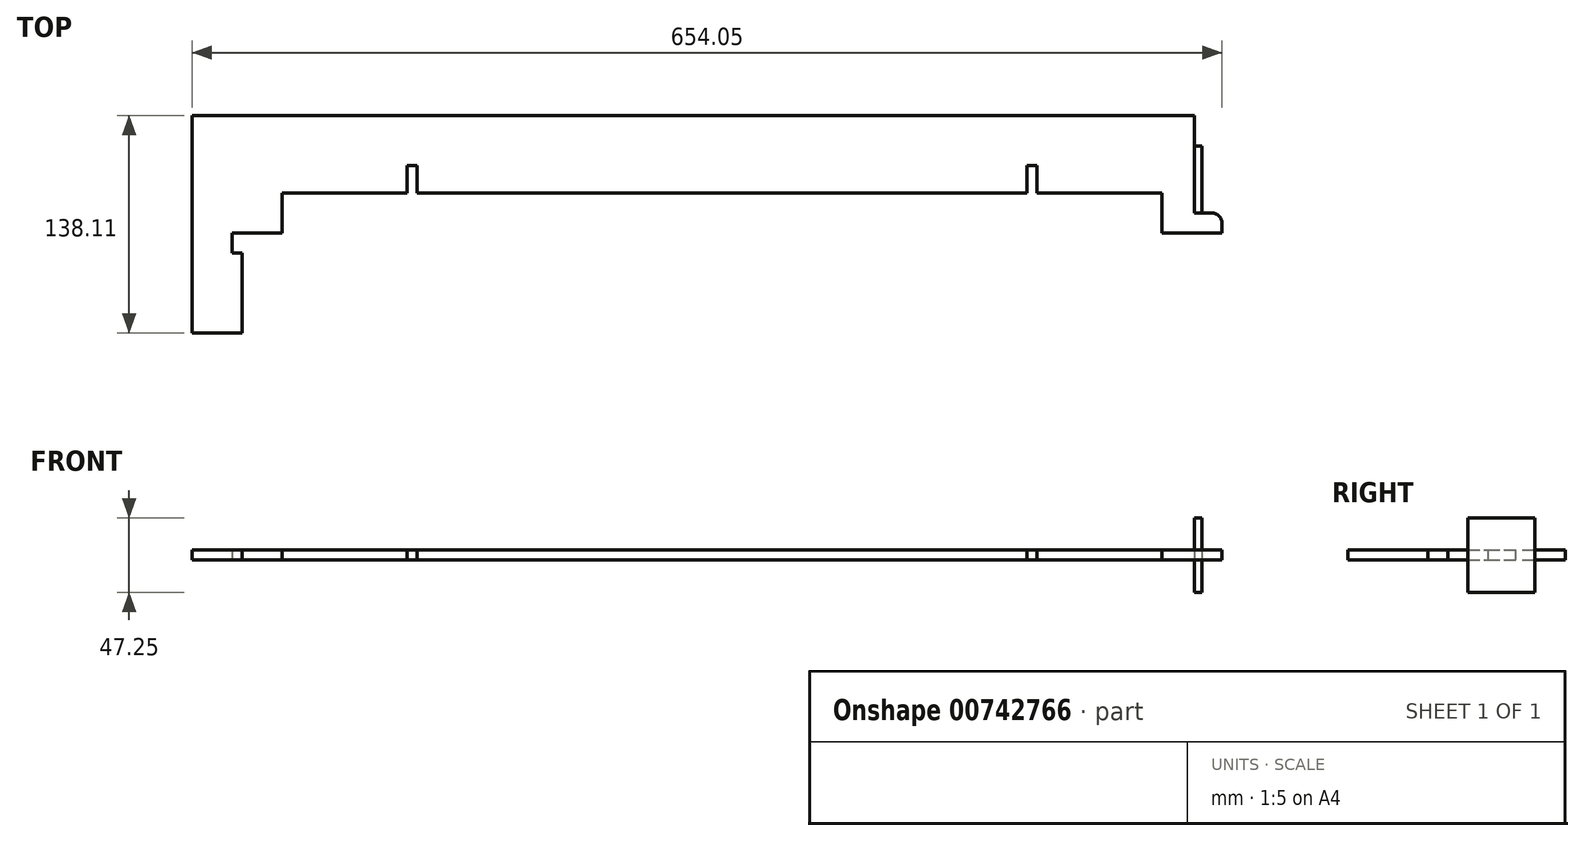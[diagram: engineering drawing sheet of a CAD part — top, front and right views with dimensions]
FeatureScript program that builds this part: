
annotation { "Feature Type Name" : "Feature", "Feature Type Description" : "" }
export const myFeature = defineFeature(function(context is Context, id is Id, definition is map)
    precondition{}
    {
        {
            var Q0;
            Q0=qCreatedBy(makeId("Top.planeOp"),FACE);
            var sketch = newSketch(context, id + "F0", { "sketchPlane" : qUnion([Q0])});
            skLineSegment(sketch, "E0.bottom", {"start": v(0, 0) * mm, "end": v(31.75, 0) * mm});
            skLineSegment(sketch, "E0.left", {"start": v(0, 0) * mm, "end": v(0, 138.11) * mm});
            skLineSegment(sketch, "E1.0", {"start": v(136.53, 106.36) * mm, "end": v(142.88, 106.36) * mm});
            skLineSegment(sketch, "E2.0", {"start": v(0, 125.41) * mm, "end": v(238.47, 125.41) * mm, "construction": true});
            skLineSegment(sketch, "E3.0", {"start": v(0, 138.11) * mm, "end": v(636.59, 138.11) * mm});
            skLineSegment(sketch, "E4.0", {"start": v(31.75, 0) * mm, "end": v(31.75, 50.8) * mm});
            skLineSegment(sketch, "E5.0", {"start": v(25.4, 63.5) * mm, "end": v(57.15, 63.5) * mm});
            skLineSegment(sketch, "E6.0", {"start": v(25.4, 50.8) * mm, "end": v(25.4, 63.5) * mm});
            skLineSegment(sketch, "E7.0", {"start": v(57.15, 63.5) * mm, "end": v(57.15, 88.9) * mm});
            skLineSegment(sketch, "E8.0", {"start": v(57.15, 88.9) * mm, "end": v(136.53, 88.9) * mm});
            skLineSegment(sketch, "E9.0", {"start": v(136.53, 88.9) * mm, "end": v(136.53, 106.36) * mm});
            skLineSegment(sketch, "E10.0", {"start": v(142.88, 88.9) * mm, "end": v(142.88, 106.36) * mm});
            skLineSegment(sketch, "E11.trimOffspring", {"start": v(142.88, 88.9) * mm, "end": v(530.23, 88.9) * mm});
            skLineSegment(sketch, "E12.0", {"start": v(536.58, 88.9) * mm, "end": v(536.58, 106.36) * mm});
            skLineSegment(sketch, "E13.0", {"start": v(530.23, 88.9) * mm, "end": v(530.23, 106.36) * mm});
            skLineSegment(sketch, "E14.trimOffspring", {"start": v(530.23, 106.36) * mm, "end": v(536.58, 106.36) * mm});
            skLineSegment(sketch, "E15.trimOffspring", {"start": v(536.58, 88.9) * mm, "end": v(615.95, 88.9) * mm});
            skLineSegment(sketch, "E16.0", {"start": v(31.75, 25.4) * mm, "end": v(641.35, 25.4) * mm, "construction": true});
            skLineSegment(sketch, "E17.0", {"start": v(615.95, 63.5) * mm, "end": v(615.95, 88.9) * mm});
            skLineSegment(sketch, "E18.trimOffspring", {"start": v(615.95, 63.5) * mm, "end": v(654.05, 63.5) * mm});
            skLineSegment(sketch, "E19.0", {"start": v(641.35, 76.2) * mm, "end": v(641.35, 118.8) * mm});
            skLineSegment(sketch, "E20.0", {"start": v(636.59, 118.8) * mm, "end": v(641.35, 118.8) * mm});
            skLineSegment(sketch, "E21.trimOffspring", {"start": v(641.35, 76.2) * mm, "end": v(654.05, 76.2) * mm});
            skLineSegment(sketch, "E22.0", {"start": v(654.05, 63.5) * mm, "end": v(654.05, 76.2) * mm});
            skLineSegment(sketch, "E23.0", {"start": v(25.4, 50.8) * mm, "end": v(31.75, 50.8) * mm});
            skLineSegment(sketch, "E24.0", {"start": v(636.59, 118.8) * mm, "end": v(636.59, 138.11) * mm});
            skSolve(sketch);
        }
        {
            var Q0;
            Q0=qSketchRegion(id+"F0",true);
            extrude(context, id + "F1", {"entities" : qUnion([Q0]), "depth" : 6.35 * mm, "offsetDistance" : 25.4 * mm});
        }
        {
            var Q0;
            Q0=makeQuery(id+"F1.opExtrude","SWEPT_FACE",FACE,{"disambiguationData":[OSD([sQuery(id+"F0.wireOp",EDGE,"E19.0")])]});
            var sketch = newSketch(context, id + "F2", { "sketchPlane" : qUnion([Q0])});
            skLineSegment(sketch, "E25.bottom", {"start": v(76.2, 26.8) * mm, "end": v(118.8, 26.8) * mm});
            skLineSegment(sketch, "E25.top", {"start": v(76.2, -20.45) * mm, "end": v(118.8, -20.45) * mm});
            skLineSegment(sketch, "E25.left", {"start": v(76.2, 26.8) * mm, "end": v(76.2, -20.45) * mm});
            skLineSegment(sketch, "E25.right", {"start": v(118.8, 26.8) * mm, "end": v(118.8, -20.45) * mm});
            skSolve(sketch);
        }
        {
            var Q0;
            Q0=qSketchRegion(id+"F2",true);
            extrude(context, id + "F3", {"entities" : qUnion([Q0]), "operationType" : NewBodyOperationType.ADD, "oppositeDirection" : true, "depth" : 4.76 * mm, "offsetDistance" : 25.4 * mm});
        }
        {
            var Q0;
            Q0=makeQuery(id+"F1.opExtrude","SWEPT_EDGE",EDGE,{"disambiguationData":[OSD([sQuery(id+"F0.wireOp",EDGE,"E21.trimOffspring"),sQuery(id+"F0.wireOp",EDGE,"E22.0")])]});
            fillet(context, id + "F4", {"entities" : qUnion([Q0]), "radius" : 6.35 * mm, "tangentPropagation" : true, "allowEdgeOverflow" : false});
        }
    });
